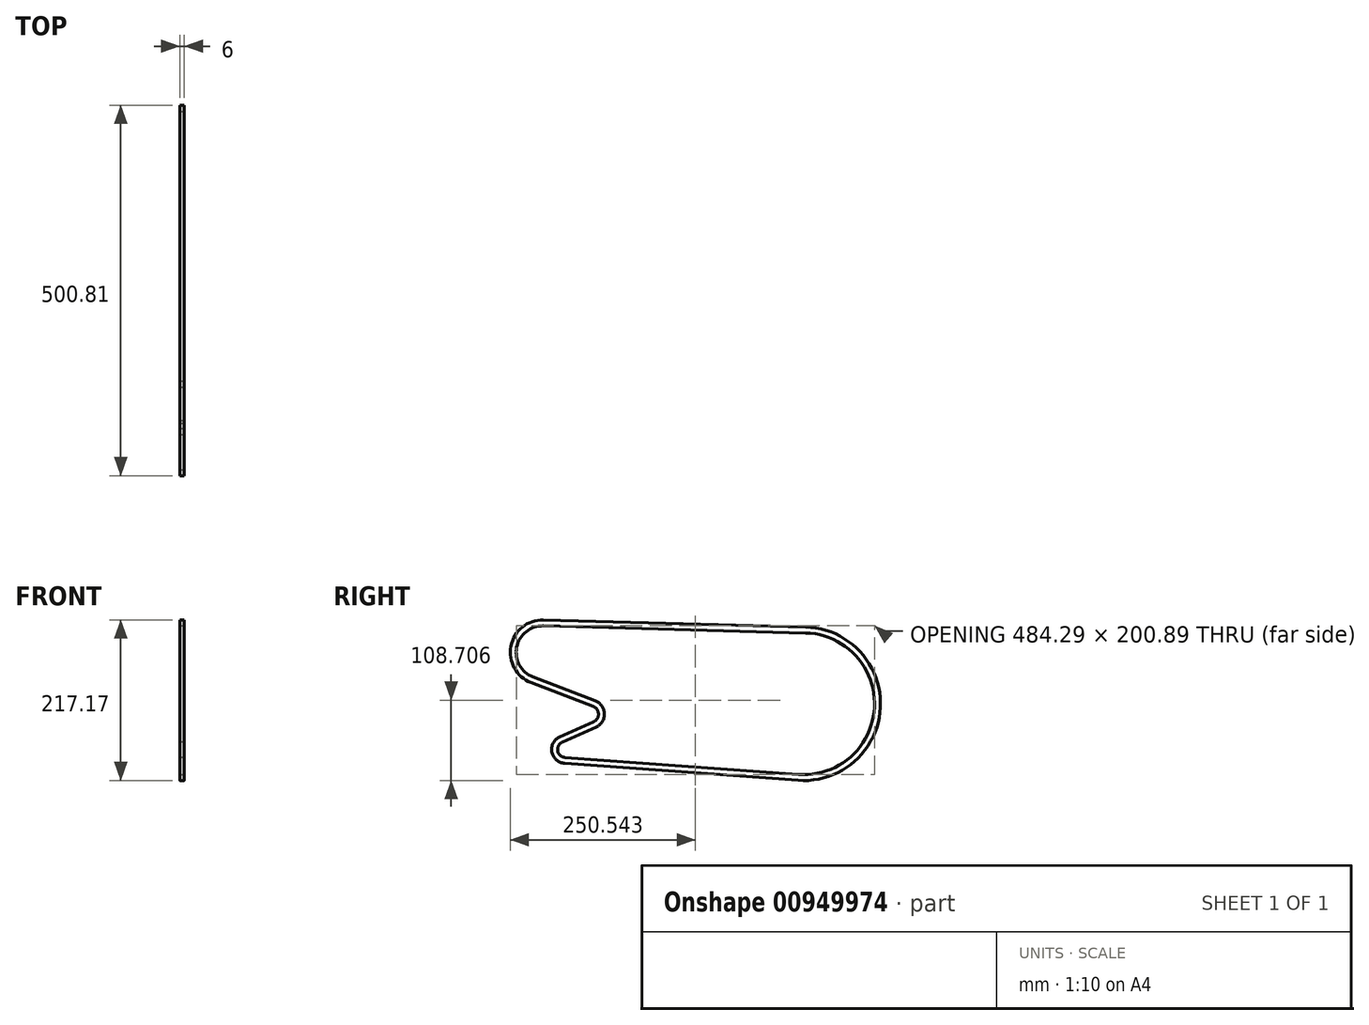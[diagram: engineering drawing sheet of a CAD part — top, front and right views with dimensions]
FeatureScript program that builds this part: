
annotation { "Feature Type Name" : "Feature", "Feature Type Description" : "" }
export const myFeature = defineFeature(function(context is Context, id is Id, definition is map)
    precondition{}
    {
        {
            var Q0;
            Q0=qCreatedBy(makeId("Right.planeOp"),FACE);
            var sketch = newSketch(context, id + "F0", { "sketchPlane" : qUnion([Q0])});
            skArc(sketch, "E0", {"start": v(-7.26, -99.74) * mm, "mid": v(99.88, -4.98) * mm, "end": v(2.7, 99.96) * mm});
            skArc(sketch, "E1", {"start": v(-352.13, 109.55) * mm, "mid": v(-392.44, 77.38) * mm, "end": v(-367.53, 32.22) * mm});
            skLineSegment(sketch, "E2", {"start": v(-352.13, 109.55) * mm, "end": v(2.7, 99.96) * mm});
            skPoint(sketch, "E3", {"position": v(-352.13, 109.55) * mm});
            skPoint(sketch, "E4", {"position": v(-367.53, 32.22) * mm});
            skPoint(sketch, "E5", {"position": v(-44.44, -89.58) * mm});
            skPoint(sketch, "E6", {"position": v(2.7, 99.96) * mm});
            skArc(sketch, "E7", {"start": v(-282.75, -27.7) * mm, "mid": v(-273.87, -13.6) * mm, "end": v(-283.5, 0) * mm});
            skArc(sketch, "E8", {"start": v(-328.33, -48.06) * mm, "mid": v(-336.98, -64.35) * mm, "end": v(-323.3, -76.72) * mm});
            skLineSegment(sketch, "E9", {"start": v(-367.53, 32.22) * mm, "end": v(-283.5, 0) * mm});
            skLineSegment(sketch, "E10", {"start": v(-323.3, -76.72) * mm, "end": v(-7.26, -99.74) * mm});
            skLineSegment(sketch, "E11", {"start": v(-328.33, -48.06) * mm, "end": v(-282.75, -27.7) * mm});
            skSolve(sketch);
        }
        {
            var Q0;
            Q0=qCreatedBy(makeId("Front.planeOp"),FACE);
            var sketch = newSketch(context, id + "F1", { "sketchPlane" : qUnion([Q0])});
            skLineSegment(sketch, "E12.bottom", {"start": v(3.2, 103.84) * mm, "end": v(-2.8, 103.84) * mm});
            skLineSegment(sketch, "E12.top", {"start": v(3.2, 95.84) * mm, "end": v(-2.8, 95.84) * mm});
            skLineSegment(sketch, "E12.left", {"start": v(3.2, 103.84) * mm, "end": v(3.2, 95.84) * mm});
            skLineSegment(sketch, "E12.right", {"start": v(-2.8, 103.84) * mm, "end": v(-2.8, 95.84) * mm});
            skSolve(sketch);
        }
        {
            var Q0;
            Q0=makeQuery(id+"F1.imprint","IMPRINT",FACE,{"disambiguationData":[TD([[makeQuery(id+"F1.imprint","IMPRINT",EDGE,{"derivedFrom":sQuery(id+"F1.wireOp",EDGE,"E12.bottom")}),1.0]])]});
            var Q1;
            Q1=sQuery(id+"F0.wireOp",EDGE,"E2");
            var Q2;
            Q2=sQuery(id+"F0.wireOp",EDGE,"E0");
            var Q3;
            Q3=sQuery(id+"F0.wireOp",EDGE,"xD74B9uP-QXV6-qiwC-RsyW-5U2eyFzenrgA");
            var Q4;
            Q4=sQuery(id+"F0.wireOp",EDGE,"E1");
            var Q5;
            Q5=sQuery(id+"F0.wireOp",EDGE,"E9");
            var Q6;
            Q6=sQuery(id+"F0.wireOp",EDGE,"E7");
            var Q7;
            Q7=sQuery(id+"F0.wireOp",EDGE,"E11");
            var Q8;
            Q8=sQuery(id+"F0.wireOp",EDGE,"E8");
            var Q9;
            Q9=sQuery(id+"F0.wireOp",EDGE,"E10");
            sweep(context, id + "F2", {"profiles" : qUnion([Q0]), "path" : qUnion([Q1, Q2, Q3, Q4, Q5, Q6, Q7, Q8, Q9])});
        }
    });
